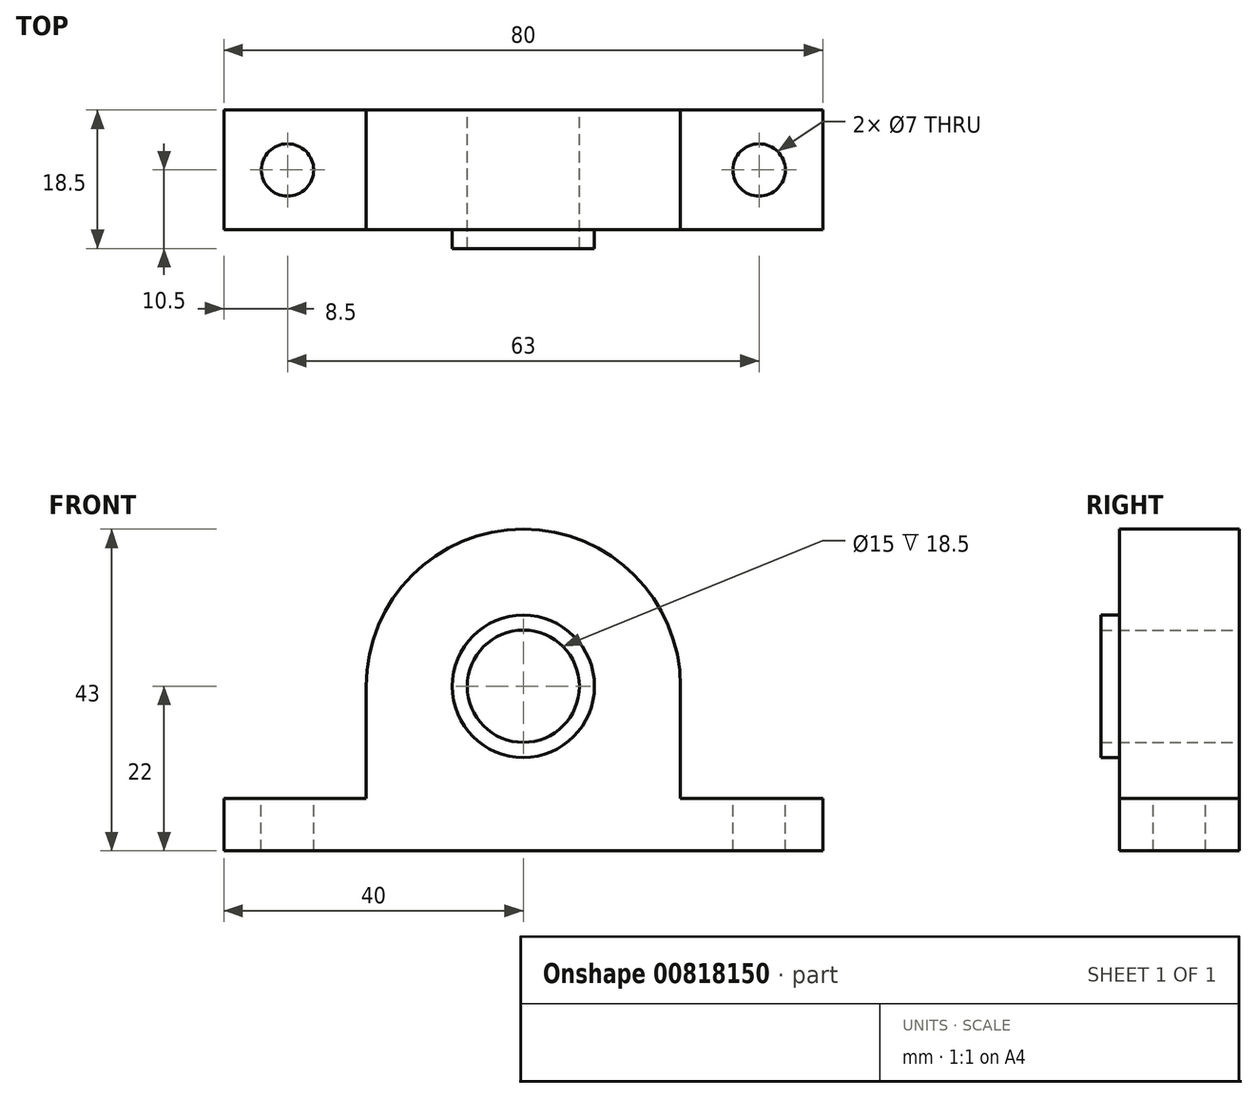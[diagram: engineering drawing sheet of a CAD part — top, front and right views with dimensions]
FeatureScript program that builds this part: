
annotation { "Feature Type Name" : "Feature", "Feature Type Description" : "" }
export const myFeature = defineFeature(function(context is Context, id is Id, definition is map)
    precondition{}
    {
        {
            var Q0;
            Q0=qCreatedBy(makeId("Front.planeOp"),FACE);
            var sketch = newSketch(context, id + "F0", { "sketchPlane" : qUnion([Q0])});
            skCircle(sketch, "E0", {"center": v(0, 0) * mm, "radius": 7.5 * mm});
            skCircle(sketch, "E1", {"center": v(0, 0) * mm, "radius": 9.5 * mm});
            skLineSegment(sketch, "E2", {"start": v(0, -22) * mm, "end": v(-40, -22) * mm});
            skLineSegment(sketch, "E3", {"start": v(-40, -22) * mm, "end": v(-40, -15) * mm});
            skLineSegment(sketch, "E4", {"start": v(-40, -15) * mm, "end": v(-21, -15) * mm});
            skLineSegment(sketch, "E5", {"start": v(-21, -15) * mm, "end": v(-21, 0) * mm});
            skArc(sketch, "E6", {"start": v(-21, 0) * mm, "mid": v(-14.85, 14.85) * mm, "end": v(0, 21) * mm});
            skLineSegment(sketch, "E7.MirrorCS", {"start": v(0, -22) * mm, "end": v(40, -22) * mm});
            skLineSegment(sketch, "E8.MirrorCS", {"start": v(40, -22) * mm, "end": v(40, -15) * mm});
            skLineSegment(sketch, "E9.MirrorCS", {"start": v(21, -15) * mm, "end": v(21, 0) * mm});
            skLineSegment(sketch, "E10.MirrorCS", {"start": v(40, -15) * mm, "end": v(21, -15) * mm});
            skArc(sketch, "E11.MirrorCS", {"start": v(21, 0) * mm, "mid": v(14.85, 14.85) * mm, "end": v(0, 21) * mm});
            skSolve(sketch);
        }
        {
            var Q0;
            Q0=makeQuery(id+"F0.imprint","IMPRINT",FACE,{"disambiguationData":[TD([[makeQuery(id+"F0.imprint","IMPRINT",EDGE,{"derivedFrom":sQuery(id+"F0.wireOp",EDGE,"E0")}),-1.0]])]});
            extrude(context, id + "F1", {"entities" : qUnion([Q0]), "depth" : 18.5 * mm, "offsetDistance" : 25 * mm});
        }
        {
            var Q0;
            Q0=makeQuery(id+"F0.imprint","IMPRINT",FACE,{"disambiguationData":[TD([[makeQuery(id+"F0.imprint","IMPRINT",EDGE,{"derivedFrom":sQuery(id+"F0.wireOp",EDGE,"E1")}),-1.0]])]});
            extrude(context, id + "F2", {"entities" : qUnion([Q0]), "operationType" : NewBodyOperationType.ADD, "depth" : 16 * mm, "offsetDistance" : 25 * mm});
        }
        {
            var Q0;
            Q0=makeQuery(id+"F2.opExtrude","SWEPT_FACE",FACE,{"disambiguationData":[OSD([sQuery(id+"F0.wireOp",EDGE,"E4")])]});
            var sketch = newSketch(context, id + "F3", { "sketchPlane" : qUnion([Q0])});
            skCircle(sketch, "E12", {"center": v(-31.5, -8) * mm, "radius": 3.5 * mm});
            skPoint(sketch, "E12.centerSnap0", {"position": v(-40, -8) * mm});
            skCircle(sketch, "E13.MirrorC", {"center": v(31.5, -8) * mm, "radius": 3.5 * mm});
            skSolve(sketch);
        }
        {
            var Q0;
            Q0 = qSketchRegion(id + "F3", true);
            extrude(context, id + "F4", {"entities" : qUnion([Q0]), "operationType" : NewBodyOperationType.REMOVE, "endBound" : BoundingType.THROUGH_ALL, "oppositeDirection" : true, "depth" : 25 * mm, "offsetDistance" : 25 * mm});
        }
    });
